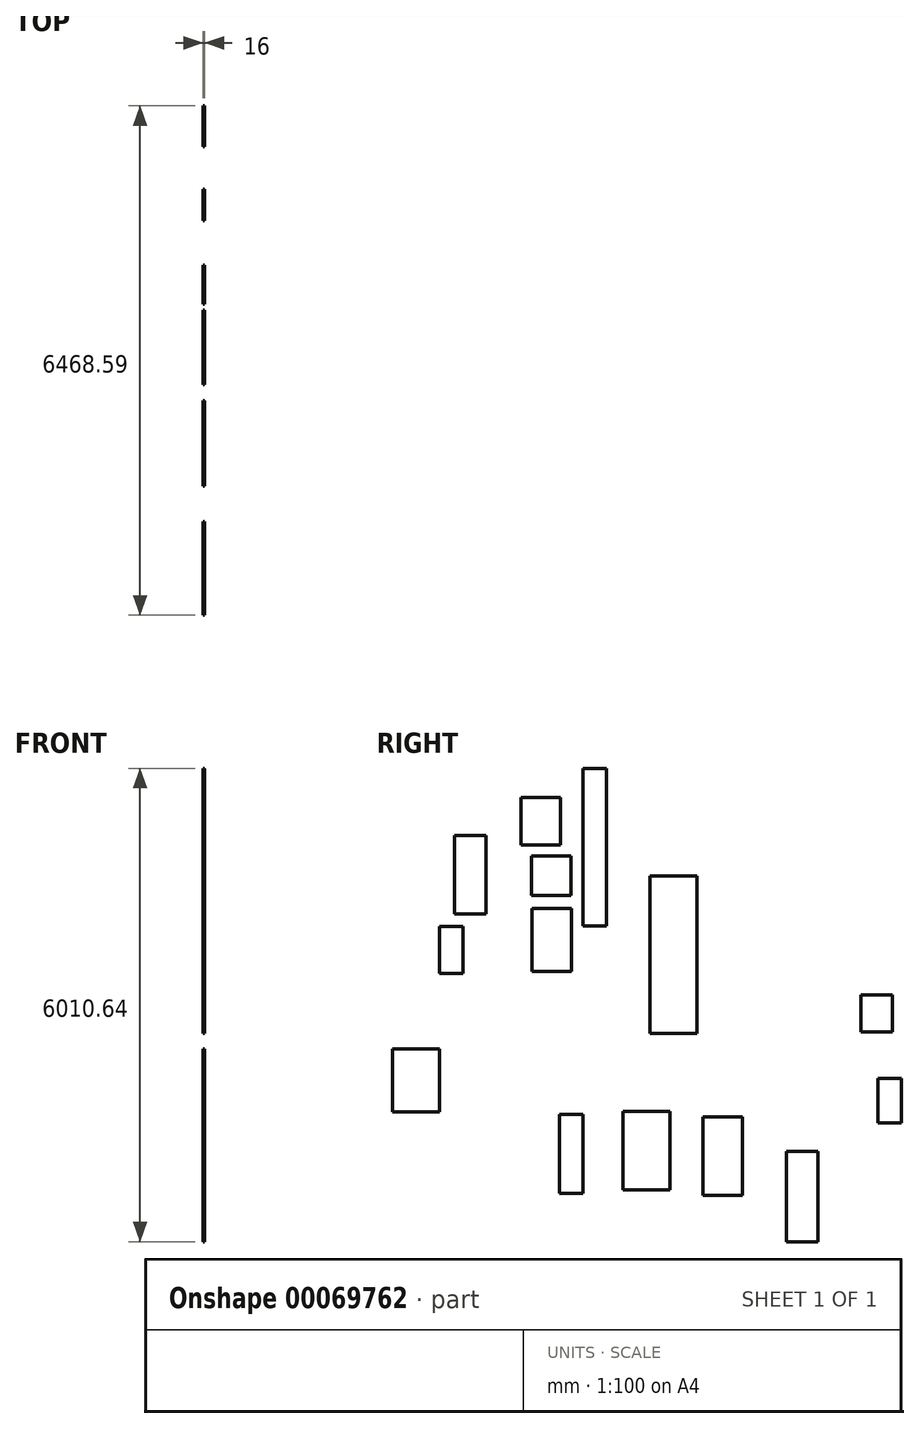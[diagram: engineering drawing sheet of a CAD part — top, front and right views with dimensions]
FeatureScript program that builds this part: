
annotation { "Feature Type Name" : "Feature", "Feature Type Description" : "" }
export const myFeature = defineFeature(function(context is Context, id is Id, definition is map)
    precondition{}
    {
        {
            var Q0;
            Q0=qCreatedBy(makeId("Right.planeOp"),FACE);
            var sketch = newSketch(context, id + "F0", { "sketchPlane" : qUnion([Q0])});
            skLineSegment(sketch, "E0.bottom", {"start": v(0, 0) * mm, "end": v(300, 0) * mm});
            skLineSegment(sketch, "E0.top", {"start": v(0, 2000) * mm, "end": v(300, 2000) * mm});
            skLineSegment(sketch, "E0.left", {"start": v(0, 0) * mm, "end": v(0, 2000) * mm});
            skLineSegment(sketch, "E0.right", {"start": v(300, 0) * mm, "end": v(300, 2000) * mm});
            skSolve(sketch);
        }
        {
            var Q0;
            Q0=makeQuery(id+"F0.imprint","IMPRINT",FACE,{"disambiguationData":[TD([[makeQuery(id+"F0.imprint","IMPRINT",EDGE,{"derivedFrom":sQuery(id+"F0.wireOp",EDGE,"E0.bottom")}),1.0]])]});
            extrude(context, id + "F1", {"entities" : qUnion([Q0]), "depth" : 16 * mm});
        }
        {
            var Q0;
            Q0=qCreatedBy(makeId("Right.planeOp"),FACE);
            var sketch = newSketch(context, id + "F2", { "sketchPlane" : qUnion([Q0])});
            skLineSegment(sketch, "E1.bottom", {"start": v(849.18, -1363.06) * mm, "end": v(1449.18, -1363.06) * mm});
            skLineSegment(sketch, "E1.top", {"start": v(849.18, 636.94) * mm, "end": v(1449.18, 636.94) * mm});
            skLineSegment(sketch, "E1.left", {"start": v(849.18, -1363.06) * mm, "end": v(849.18, 636.94) * mm});
            skLineSegment(sketch, "E1.right", {"start": v(1449.18, -1363.06) * mm, "end": v(1449.18, 636.94) * mm});
            skSolve(sketch);
        }
        {
            var Q0;
            Q0=makeQuery(id+"F2.imprint","IMPRINT",FACE,{"disambiguationData":[TD([[makeQuery(id+"F2.imprint","IMPRINT",EDGE,{"derivedFrom":sQuery(id+"F2.wireOp",EDGE,"E1.bottom")}),1.0]])]});
            extrude(context, id + "F3", {"entities" : qUnion([Q0]), "depth" : 16 * mm});
        }
        {
            var Q0;
            Q0=qCreatedBy(makeId("Right.planeOp"),FACE);
            var sketch = newSketch(context, id + "F4", { "sketchPlane" : qUnion([Q0])});
            skLineSegment(sketch, "E2.bottom", {"start": v(-644.62, -577.55) * mm, "end": v(-144.62, -577.55) * mm});
            skLineSegment(sketch, "E2.top", {"start": v(-644.62, 222.45) * mm, "end": v(-144.62, 222.45) * mm});
            skLineSegment(sketch, "E2.left", {"start": v(-644.62, -577.55) * mm, "end": v(-644.62, 222.45) * mm});
            skLineSegment(sketch, "E2.right", {"start": v(-144.62, -577.55) * mm, "end": v(-144.62, 222.45) * mm});
            skSolve(sketch);
        }
        {
            var Q0;
            Q0=makeQuery(id+"F4.imprint","IMPRINT",FACE,{"disambiguationData":[TD([[makeQuery(id+"F4.imprint","IMPRINT",EDGE,{"derivedFrom":sQuery(id+"F4.wireOp",EDGE,"E2.bottom")}),1.0]])]});
            extrude(context, id + "F5", {"entities" : qUnion([Q0]), "depth" : 16 * mm});
        }
        {
            var Q0;
            Q0=qCreatedBy(makeId("Right.planeOp"),FACE);
            var sketch = newSketch(context, id + "F6", { "sketchPlane" : qUnion([Q0])});
            skLineSegment(sketch, "E3.bottom", {"start": v(-652, 387.91) * mm, "end": v(-152, 387.91) * mm});
            skLineSegment(sketch, "E3.top", {"start": v(-652, 887.91) * mm, "end": v(-152, 887.91) * mm});
            skLineSegment(sketch, "E3.left", {"start": v(-652, 387.91) * mm, "end": v(-652, 887.91) * mm});
            skLineSegment(sketch, "E3.right", {"start": v(-152, 387.91) * mm, "end": v(-152, 887.91) * mm});
            skSolve(sketch);
        }
        {
            var Q0;
            Q0 = qSketchRegion(id + "F6", true);
            extrude(context, id + "F7", {"entities" : qUnion([Q0]), "depth" : 16 * mm});
        }
        {
            var Q0;
            Q0=qCreatedBy(makeId("Right.planeOp"),FACE);
            var sketch = newSketch(context, id + "F8", { "sketchPlane" : qUnion([Q0])});
            skLineSegment(sketch, "E4.bottom", {"start": v(-785.4, 1630.2) * mm, "end": v(-285.4, 1630.2) * mm});
            skLineSegment(sketch, "E4.top", {"start": v(-785.4, 1030.2) * mm, "end": v(-285.4, 1030.2) * mm});
            skLineSegment(sketch, "E4.left", {"start": v(-785.4, 1630.2) * mm, "end": v(-785.4, 1030.2) * mm});
            skLineSegment(sketch, "E4.right", {"start": v(-285.4, 1630.2) * mm, "end": v(-285.4, 1030.2) * mm});
            skSolve(sketch);
        }
        {
            var Q0;
            Q0 = qSketchRegion(id + "F8", true);
            extrude(context, id + "F9", {"entities" : qUnion([Q0]), "depth" : 16 * mm});
        }
        {
            var Q0;
            Q0=qCreatedBy(makeId("Right.planeOp"),FACE);
            var sketch = newSketch(context, id + "F10", { "sketchPlane" : qUnion([Q0])});
            skLineSegment(sketch, "E5.bottom", {"start": v(-1820.79, -3.44) * mm, "end": v(-1520.79, -3.44) * mm});
            skLineSegment(sketch, "E5.top", {"start": v(-1820.79, -603.44) * mm, "end": v(-1520.79, -603.44) * mm});
            skLineSegment(sketch, "E5.left", {"start": v(-1820.79, -3.44) * mm, "end": v(-1820.79, -603.44) * mm});
            skLineSegment(sketch, "E5.right", {"start": v(-1520.79, -3.44) * mm, "end": v(-1520.79, -603.44) * mm});
            skSolve(sketch);
        }
        {
            var Q0;
            Q0 = qSketchRegion(id + "F10", true);
            extrude(context, id + "F11", {"entities" : qUnion([Q0]), "depth" : 16 * mm});
        }
        {
            var Q0;
            Q0=qCreatedBy(makeId("Right.planeOp"),FACE);
            var sketch = newSketch(context, id + "F12", { "sketchPlane" : qUnion([Q0])});
            skLineSegment(sketch, "E6.bottom", {"start": v(-1631.86, 149.98) * mm, "end": v(-1231.86, 149.98) * mm});
            skLineSegment(sketch, "E6.top", {"start": v(-1631.86, 1149.98) * mm, "end": v(-1231.86, 1149.98) * mm});
            skLineSegment(sketch, "E6.left", {"start": v(-1631.86, 149.98) * mm, "end": v(-1631.86, 1149.98) * mm});
            skLineSegment(sketch, "E6.right", {"start": v(-1231.86, 149.98) * mm, "end": v(-1231.86, 1149.98) * mm});
            skSolve(sketch);
        }
        {
            var Q0;
            Q0=makeQuery(id+"F12.imprint","IMPRINT",FACE,{"disambiguationData":[TD([[makeQuery(id+"F12.imprint","IMPRINT",EDGE,{"derivedFrom":sQuery(id+"F12.wireOp",EDGE,"E6.bottom")}),1.0]])]});
            extrude(context, id + "F13", {"entities" : qUnion([Q0]), "depth" : 16 * mm, "offsetDistance" : 25 * mm});
        }
        {
            var Q0;
            Q0=qCreatedBy(makeId("Right.planeOp"),FACE);
            var sketch = newSketch(context, id + "F14", { "sketchPlane" : qUnion([Q0])});
            skLineSegment(sketch, "E7.bottom", {"start": v(-300, -2396.12) * mm, "end": v(0, -2396.12) * mm});
            skLineSegment(sketch, "E7.top", {"start": v(-300, -3396.12) * mm, "end": v(0, -3396.12) * mm});
            skLineSegment(sketch, "E7.left", {"start": v(-300, -2396.12) * mm, "end": v(-300, -3396.12) * mm});
            skLineSegment(sketch, "E7.right", {"start": v(0, -2396.12) * mm, "end": v(0, -3396.12) * mm});
            skSolve(sketch);
        }
        {
            var Q0;
            Q0=makeQuery(id+"F14.imprint","IMPRINT",FACE,{"disambiguationData":[TD([[makeQuery(id+"F14.imprint","IMPRINT",EDGE,{"derivedFrom":sQuery(id+"F14.wireOp",EDGE,"E7.bottom")}),-1.0]])]});
            extrude(context, id + "F15", {"entities" : qUnion([Q0]), "depth" : 16 * mm, "offsetDistance" : 25 * mm});
        }
        {
            var Q0;
            Q0=qCreatedBy(makeId("Right.planeOp"),FACE);
            var sketch = newSketch(context, id + "F16", { "sketchPlane" : qUnion([Q0])});
            skLineSegment(sketch, "E8.bottom", {"start": v(1525.47, -2424.92) * mm, "end": v(2025.47, -2424.92) * mm});
            skLineSegment(sketch, "E8.top", {"start": v(1525.47, -3424.92) * mm, "end": v(2025.47, -3424.92) * mm});
            skLineSegment(sketch, "E8.left", {"start": v(1525.47, -2424.92) * mm, "end": v(1525.47, -3424.92) * mm});
            skLineSegment(sketch, "E8.right", {"start": v(2025.47, -2424.92) * mm, "end": v(2025.47, -3424.92) * mm});
            skSolve(sketch);
        }
        {
            var Q0;
            Q0 = qSketchRegion(id + "F16", true);
            extrude(context, id + "F17", {"entities" : qUnion([Q0]), "depth" : 16 * mm, "offsetDistance" : 25 * mm});
        }
        {
            var Q0;
            Q0=qCreatedBy(makeId("Right.planeOp"),FACE);
            var sketch = newSketch(context, id + "F18", { "sketchPlane" : qUnion([Q0])});
            skLineSegment(sketch, "E9.bottom", {"start": v(508.39, -2355.24) * mm, "end": v(1108.39, -2355.24) * mm});
            skLineSegment(sketch, "E9.top", {"start": v(508.39, -3355.24) * mm, "end": v(1108.39, -3355.24) * mm});
            skLineSegment(sketch, "E9.left", {"start": v(508.39, -2355.24) * mm, "end": v(508.39, -3355.24) * mm});
            skLineSegment(sketch, "E9.right", {"start": v(1108.39, -2355.24) * mm, "end": v(1108.39, -3355.24) * mm});
            skSolve(sketch);
        }
        {
            var Q0;
            Q0=makeQuery(id+"F18.imprint","IMPRINT",FACE,{"disambiguationData":[TD([[makeQuery(id+"F18.imprint","IMPRINT",EDGE,{"derivedFrom":sQuery(id+"F18.wireOp",EDGE,"E9.bottom")}),-1.0]])]});
            extrude(context, id + "F19", {"entities" : qUnion([Q0]), "depth" : 16 * mm, "offsetDistance" : 25 * mm});
        }
        {
            var Q0;
            Q0=qCreatedBy(makeId("Right.planeOp"),FACE);
            var sketch = newSketch(context, id + "F20", { "sketchPlane" : qUnion([Q0])});
            skLineSegment(sketch, "E10.bottom", {"start": v(-2421.29, -1559.85) * mm, "end": v(-1821.29, -1559.85) * mm});
            skLineSegment(sketch, "E10.top", {"start": v(-2421.29, -2359.85) * mm, "end": v(-1821.29, -2359.85) * mm});
            skLineSegment(sketch, "E10.left", {"start": v(-2421.29, -1559.85) * mm, "end": v(-2421.29, -2359.85) * mm});
            skLineSegment(sketch, "E10.right", {"start": v(-1821.29, -1559.85) * mm, "end": v(-1821.29, -2359.85) * mm});
            skSolve(sketch);
        }
        {
            var Q0;
            Q0=makeQuery(id+"F20.imprint","IMPRINT",FACE,{"disambiguationData":[TD([[makeQuery(id+"F20.imprint","IMPRINT",EDGE,{"derivedFrom":sQuery(id+"F20.wireOp",EDGE,"E10.bottom")}),-1.0]])]});
            extrude(context, id + "F21", {"entities" : qUnion([Q0]), "depth" : 16 * mm, "offsetDistance" : 25 * mm});
        }
        {
            var Q0;
            Q0=qCreatedBy(makeId("Right.planeOp"),FACE);
            var sketch = newSketch(context, id + "F22", { "sketchPlane" : qUnion([Q0])});
            skLineSegment(sketch, "E11.bottom", {"start": v(3531.1, -878.8) * mm, "end": v(3931.1, -878.8) * mm});
            skLineSegment(sketch, "E11.top", {"start": v(3531.1, -1346.8) * mm, "end": v(3931.1, -1346.8) * mm});
            skLineSegment(sketch, "E11.left", {"start": v(3531.1, -878.8) * mm, "end": v(3531.1, -1346.8) * mm});
            skLineSegment(sketch, "E11.right", {"start": v(3931.1, -878.8) * mm, "end": v(3931.1, -1346.8) * mm});
            skSolve(sketch);
        }
        {
            var Q0;
            Q0=makeQuery(id+"F22.imprint","IMPRINT",FACE,{"disambiguationData":[TD([[makeQuery(id+"F22.imprint","IMPRINT",EDGE,{"derivedFrom":sQuery(id+"F22.wireOp",EDGE,"E11.bottom")}),-1.0]])]});
            extrude(context, id + "F23", {"entities" : qUnion([Q0]), "depth" : 16 * mm, "offsetDistance" : 25 * mm});
        }
        {
            var Q0;
            Q0=qCreatedBy(makeId("Right.planeOp"),FACE);
            var sketch = newSketch(context, id + "F24", { "sketchPlane" : qUnion([Q0])});
            skLineSegment(sketch, "E12.bottom", {"start": v(3747.3, -1936.33) * mm, "end": v(4047.3, -1936.33) * mm});
            skLineSegment(sketch, "E12.top", {"start": v(3747.3, -2504.33) * mm, "end": v(4047.3, -2504.33) * mm});
            skLineSegment(sketch, "E12.left", {"start": v(3747.3, -1936.33) * mm, "end": v(3747.3, -2504.33) * mm});
            skLineSegment(sketch, "E12.right", {"start": v(4047.3, -1936.33) * mm, "end": v(4047.3, -2504.33) * mm});
            skSolve(sketch);
        }
        {
            var Q0;
            Q0=makeQuery(id+"F24.imprint","IMPRINT",FACE,{"disambiguationData":[TD([[makeQuery(id+"F24.imprint","IMPRINT",EDGE,{"derivedFrom":sQuery(id+"F24.wireOp",EDGE,"E12.bottom")}),-1.0]])]});
            extrude(context, id + "F25", {"entities" : qUnion([Q0]), "depth" : 16 * mm, "offsetDistance" : 25 * mm});
        }
        {
            var Q0;
            Q0=qCreatedBy(makeId("Right.planeOp"),FACE);
            var sketch = newSketch(context, id + "F26", { "sketchPlane" : qUnion([Q0])});
            skLineSegment(sketch, "E13.bottom", {"start": v(2588.26, -2860.64) * mm, "end": v(2988.26, -2860.64) * mm});
            skLineSegment(sketch, "E13.top", {"start": v(2588.26, -4010.64) * mm, "end": v(2988.26, -4010.64) * mm});
            skLineSegment(sketch, "E13.left", {"start": v(2588.26, -2860.64) * mm, "end": v(2588.26, -4010.64) * mm});
            skLineSegment(sketch, "E13.right", {"start": v(2988.26, -2860.64) * mm, "end": v(2988.26, -4010.64) * mm});
            skSolve(sketch);
        }
        {
            var Q0;
            Q0=makeQuery(id+"F26.imprint","IMPRINT",FACE,{"disambiguationData":[TD([[makeQuery(id+"F26.imprint","IMPRINT",EDGE,{"derivedFrom":sQuery(id+"F26.wireOp",EDGE,"E13.bottom")}),-1.0]])]});
            extrude(context, id + "F27", {"entities" : qUnion([Q0]), "depth" : 16 * mm, "offsetDistance" : 25 * mm});
        }
    });
